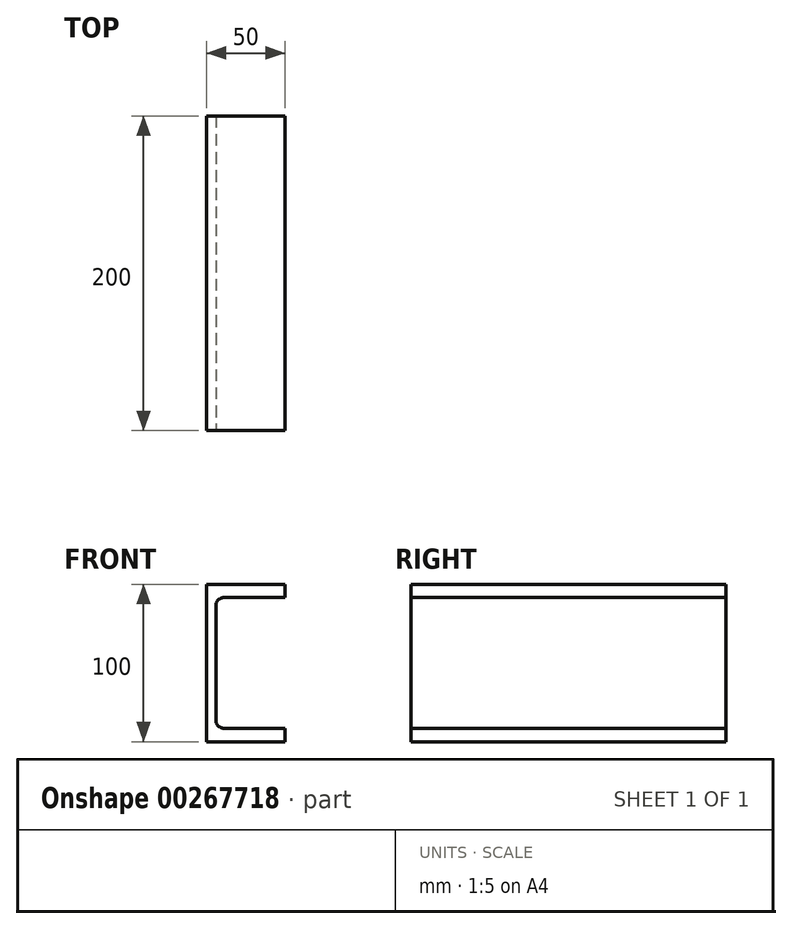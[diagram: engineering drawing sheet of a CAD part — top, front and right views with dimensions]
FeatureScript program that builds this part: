
annotation { "Feature Type Name" : "Feature", "Feature Type Description" : "" }
export const myFeature = defineFeature(function(context is Context, id is Id, definition is map)
    precondition{}
    {
        {
            var Q0;
            Q0=qCreatedBy(makeId("Front.planeOp"),FACE);
            var sketch = newSketch(context, id + "F0", { "sketchPlane" : qUnion([Q0])});
            skLineSegment(sketch, "E0.bottom", {"start": v(25, 50) * mm, "end": v(-25, 50) * mm});
            skLineSegment(sketch, "E0.top", {"start": v(25, -50) * mm, "end": v(-25, -50) * mm});
            skLineSegment(sketch, "E0.left", {"start": v(25, 50) * mm, "end": v(25, -50) * mm});
            skLineSegment(sketch, "E0.right", {"start": v(-25, 50) * mm, "end": v(-25, -50) * mm});
            skPoint(sketch, "E0.middle", {"position": v(0, 0) * mm});
            skLineSegment(sketch, "E1.0", {"start": v(25, 41.5) * mm, "end": v(-14, 41.5) * mm});
            skLineSegment(sketch, "E2.0", {"start": v(25, -41.5) * mm, "end": v(-14, -41.5) * mm});
            skLineSegment(sketch, "E3.0", {"start": v(-19, 36.5) * mm, "end": v(-19, -36.5) * mm});
            skArc(sketch, "E4.filletArc", {"start": v(-14, 41.5) * mm, "mid": v(-17.54, 40.04) * mm, "end": v(-19, 36.5) * mm});
            skArc(sketch, "E5.filletArc", {"start": v(-19, -36.5) * mm, "mid": v(-17.54, -40.04) * mm, "end": v(-14, -41.5) * mm});
            skSolve(sketch);
        }
        {
            var Q0;
            {var subQ3=sQuery(id+"F0.wireOp",EDGE,"E0.bottom");Q0=makeQuery(id+"F0.imprint","IMPRINT",FACE,{"disambiguationData":[TD([[makeQuery(id+"F0.imprint","IMPRINT",EDGE,{"derivedFrom":subQ3}),1.0]])]});}
            extrude(context, id + "F1", {"entities" : qUnion([Q0]), "oppositeDirection" : true, "depth" : 200 * mm});
        }
    });
